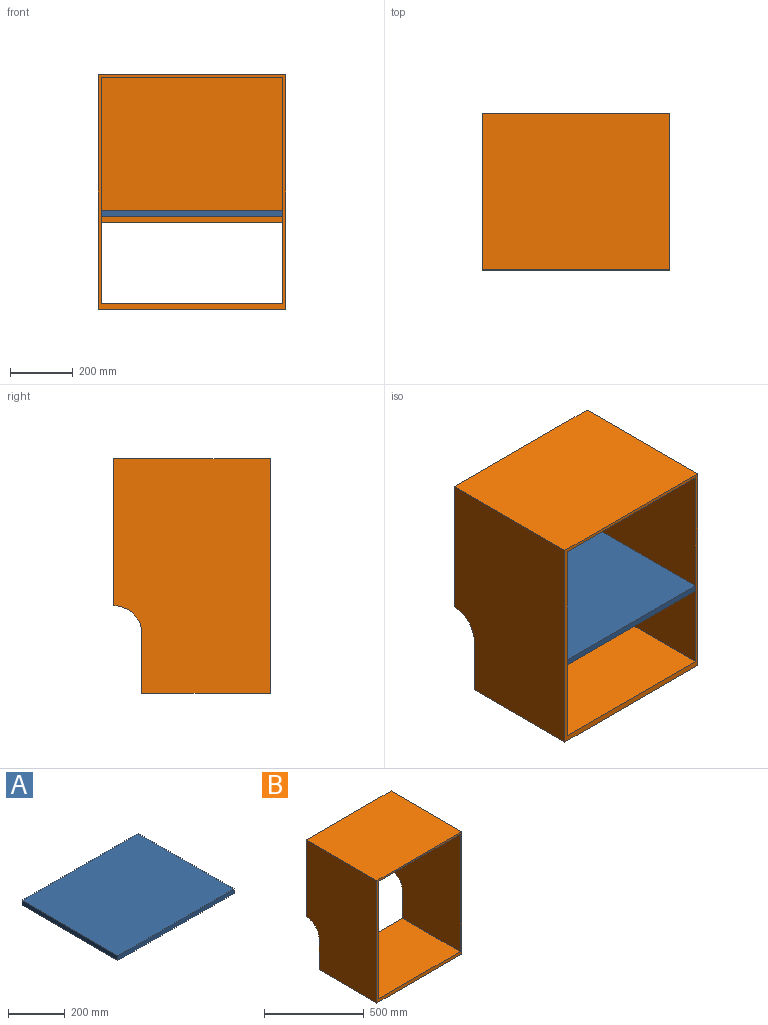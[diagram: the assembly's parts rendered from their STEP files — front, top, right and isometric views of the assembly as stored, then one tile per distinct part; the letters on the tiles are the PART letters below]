
ASSEMBLY  parts=2 mates=1
PART A: 6 faces, bbox 580x480x20 mm
  f0: plane 480x20mm, normal (1,0,0), area 9600mm2, adj f1,f3,f4,f5
  f1: plane 580x20mm, normal (0,1,0), area 11600mm2, adj f0,f2,f4,f5
  f2: plane 480x20mm, normal (-1,0,0), area 9600mm2, adj f1,f3,f4,f5
  f3: plane 580x20mm, normal (0,-1,0), area 11600mm2, adj f0,f2,f4,f5
  f4: plane 580x480mm, normal (0,0,1), area 278400mm2, adj f0,f1,f2,f3
  f5: plane 580x480mm, normal (0,0,-1), area 278400mm2, adj f0,f1,f2,f3
PART B: 13 faces, bbox 600x500x750 mm
  f0: plane 580x410mm, normal (0,0,1), area 237800mm2, adj f2,f9,f10,f11
  f1: plane 580x462.25mm, normal (0,-1,0), area 268105.2mm2, adj f8,f9,f10,f12
  f2: plane 750x600mm, normal (0,-1,0), area 32400mm2, adj f0,f4,f5,f6,f7,f8,f9,f10
  f3: plane 600x470mm, normal (0,1,0), area 282000mm2, adj f4,f5,f6,f12
  f4: plane 750x500mm, normal (-1,0,0), area 351538.3mm2, adj f2,f3,f6,f7,f11,f12
  f5: plane 750x500mm, normal (1,0,0), area 351538.3mm2, adj f2,f3,f6,f7,f11,f12
  f6: plane 600x500mm, normal (0,0,1), area 300000mm2, adj f2,f3,f4,f5
  f7: plane 600x410mm, normal (0,0,-1), area 246000mm2, adj f2,f4,f5,f11
  f8: plane 580x480mm, normal (0,0,-1), area 278400mm2, adj f1,f2,f9,f10
  f9: plane 720x480mm, normal (1,0,0), area 329123.3mm2, adj f0,f1,f2,f8,f11,f12
  f10: plane 720x480mm, normal (-1,0,0), area 329123.3mm2, adj f0,f1,f2,f8,f11,f12
  f11: plane 600x190mm, normal (0,1,0), area 15400mm2, adj f0,f4,f5,f7,f9,f10,f12
  f12: cylinder r=90mm len=600mm, axis (1,0,0), area 14525.1mm2, adj f1,f3,f4,f5,f9,f10,f11
PLACE A t=(-10,-0.34,-97.91)mm
PLACE B t=(-310,260,-395)mm fixed
MATE fastened B.f9 <-> A.f2  axis (1,0,0) through (-300,-10.34,-2.91)mm
